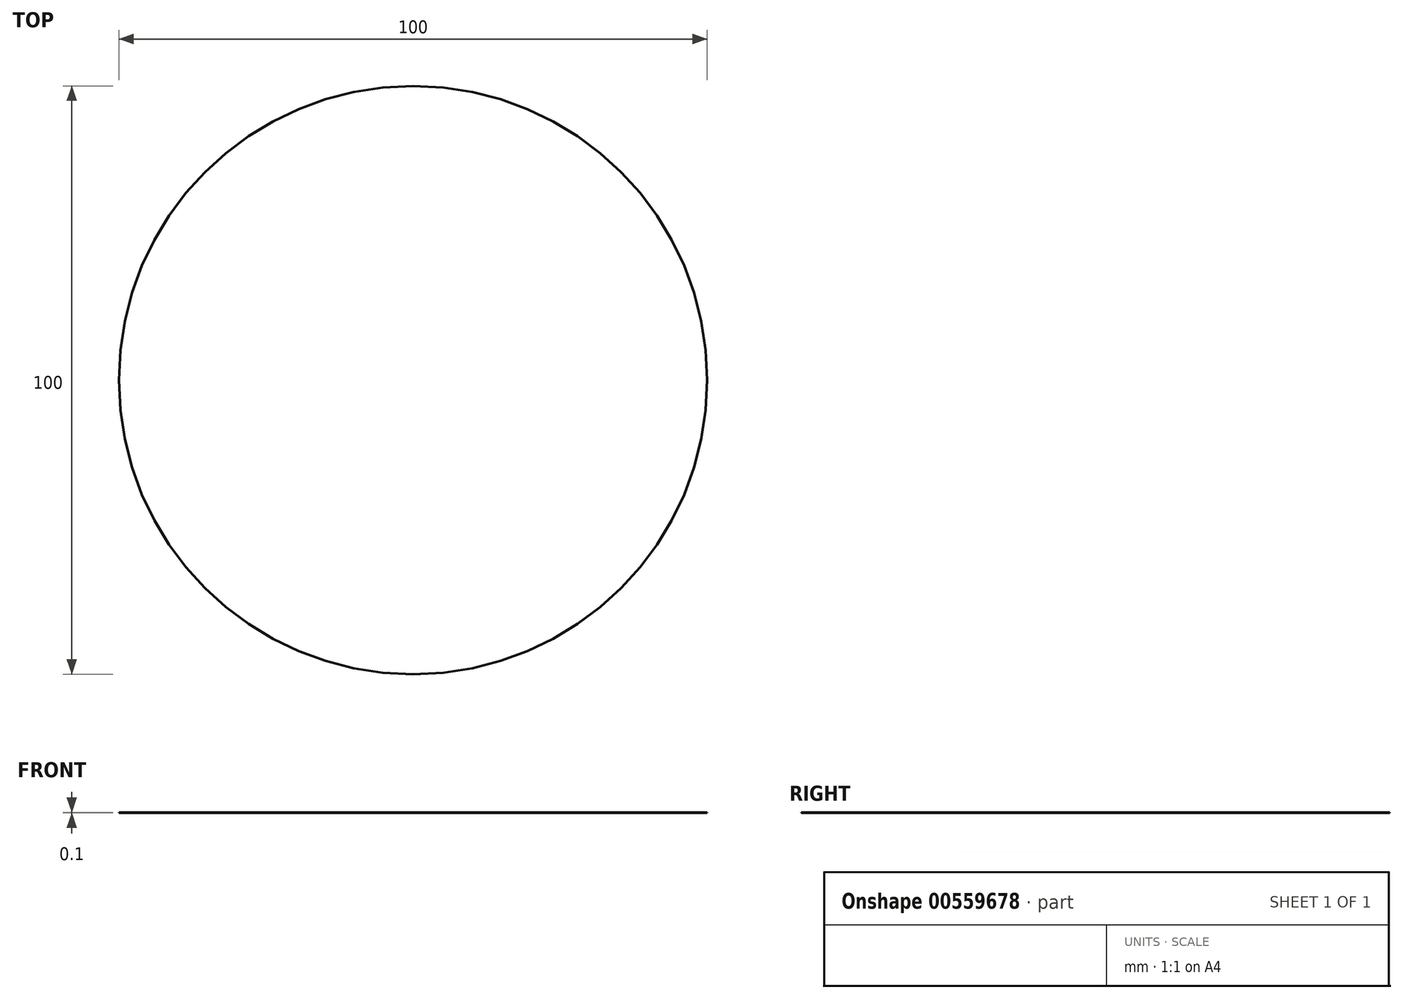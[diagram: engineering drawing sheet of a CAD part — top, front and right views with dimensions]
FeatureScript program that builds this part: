
annotation { "Feature Type Name" : "Feature", "Feature Type Description" : "" }
export const myFeature = defineFeature(function(context is Context, id is Id, definition is map)
    precondition{}
    {
        {
            var Q0;
            Q0=qCreatedBy(makeId("Top.planeOp"),FACE);
            var sketch = newSketch(context, id + "F0", { "sketchPlane" : qUnion([Q0])});
            skCircle(sketch, "E0", {"center": v(0, 0) * mm, "radius": 50 * mm});
            skSolve(sketch);
        }
        {
            var Q0;
            Q0=sQuery(id+"F0.wireOp",EDGE,"E0");
            extrude(context, id + "F1", {"bodyType" : ToolBodyType.SURFACE, "surfaceEntities" : qUnion([Q0]), "depth" : 0.1 * mm, "offsetDistance" : 25 * mm});
        }
    });
